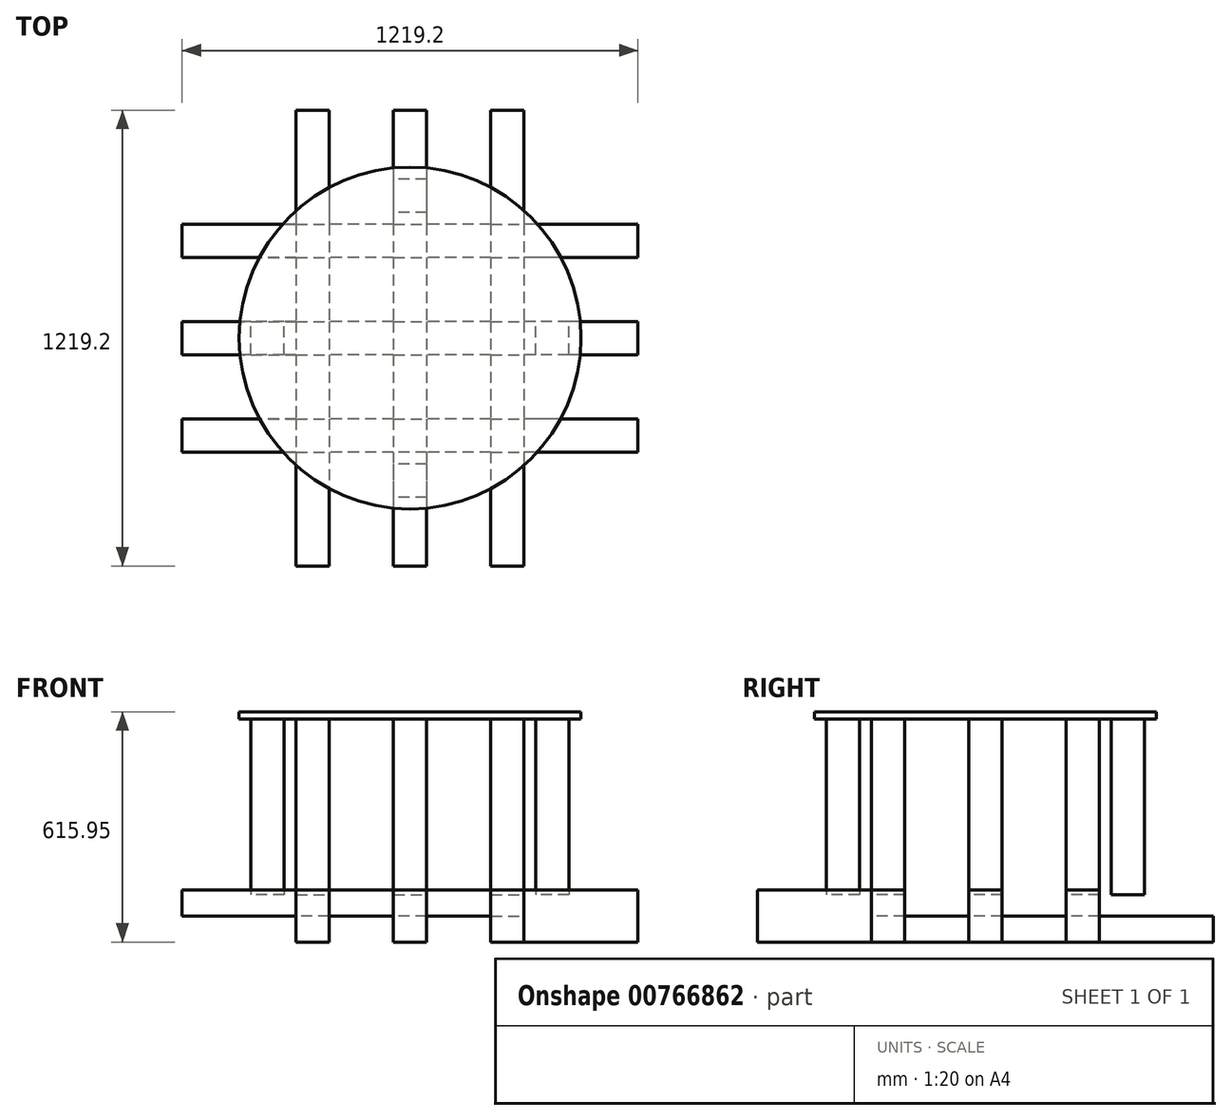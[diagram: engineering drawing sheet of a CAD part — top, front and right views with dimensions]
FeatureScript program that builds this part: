
annotation { "Feature Type Name" : "Feature", "Feature Type Description" : "" }
export const myFeature = defineFeature(function(context is Context, id is Id, definition is map)
    precondition{}
    {
        {
            var Q0;
            Q0=qCreatedBy(makeId("Top.planeOp"),FACE);
            var sketch = newSketch(context, id + "F0", { "sketchPlane" : qUnion([Q0])});
            skCircle(sketch, "E0", {"center": v(0, 0) * mm, "radius": 381 * mm, "construction": true});
            skLineSegment(sketch, "E1.bottom", {"start": v(-44.45, 609.6) * mm, "end": v(44.45, 609.6) * mm});
            skLineSegment(sketch, "E1.top", {"start": v(-44.45, -609.6) * mm, "end": v(44.45, -609.6) * mm});
            skLineSegment(sketch, "E1.left", {"start": v(-44.45, 609.6) * mm, "end": v(-44.45, -609.6) * mm});
            skLineSegment(sketch, "E1.right", {"start": v(44.45, 609.6) * mm, "end": v(44.45, -609.6) * mm});
            skLineSegment(sketch, "E2", {"start": v(0, 0) * mm, "end": v(260.35, 0) * mm, "construction": true});
            skLineSegment(sketch, "E3", {"start": v(0, 0) * mm, "end": v(-260.35, 0) * mm, "construction": true});
            skPoint(sketch, "E3.endSnap0", {"position": v(-44.45, 0) * mm});
            skLineSegment(sketch, "E4.bottom", {"start": v(-304.8, 609.6) * mm, "end": v(-215.9, 609.6) * mm});
            skLineSegment(sketch, "E4.top", {"start": v(-304.8, -609.6) * mm, "end": v(-215.9, -609.6) * mm});
            skLineSegment(sketch, "E4.left", {"start": v(-304.8, 609.6) * mm, "end": v(-304.8, -609.6) * mm});
            skLineSegment(sketch, "E4.right", {"start": v(-215.9, 609.6) * mm, "end": v(-215.9, -609.6) * mm});
            skPoint(sketch, "E4.middle", {"position": v(-260.35, 0) * mm});
            skLineSegment(sketch, "E5.bottom", {"start": v(215.9, 609.6) * mm, "end": v(304.8, 609.6) * mm});
            skLineSegment(sketch, "E5.top", {"start": v(215.9, -609.6) * mm, "end": v(304.8, -609.6) * mm});
            skLineSegment(sketch, "E5.left", {"start": v(215.9, 609.6) * mm, "end": v(215.9, -609.6) * mm});
            skLineSegment(sketch, "E5.right", {"start": v(304.8, 609.6) * mm, "end": v(304.8, -304.8) * mm});
            skPoint(sketch, "E5.middle", {"position": v(260.35, 0) * mm});
            skPoint(sketch, "E5.cornerSnap0", {"position": v(-260.35, 609.6) * mm});
            skLineSegment(sketch, "E6", {"start": v(0, 0) * mm, "end": v(0, 260.35) * mm, "construction": true});
            skLineSegment(sketch, "E7", {"start": v(0, 0) * mm, "end": v(0, -260.35) * mm, "construction": true});
            skLineSegment(sketch, "E8.bottom", {"start": v(609.6, 304.8) * mm, "end": v(-304.8, 304.8) * mm});
            skLineSegment(sketch, "E8.top", {"start": v(609.6, 215.9) * mm, "end": v(-609.6, 215.9) * mm});
            skLineSegment(sketch, "E8.left", {"start": v(609.6, 304.8) * mm, "end": v(609.6, 215.9) * mm});
            skLineSegment(sketch, "E8.right", {"start": v(-609.6, 304.8) * mm, "end": v(-609.6, 215.9) * mm});
            skPoint(sketch, "E8.middle", {"position": v(0, 260.35) * mm});
            skLineSegment(sketch, "E9.bottom", {"start": v(609.6, -215.9) * mm, "end": v(-609.6, -215.9) * mm});
            skLineSegment(sketch, "E9.top", {"start": v(609.6, -304.8) * mm, "end": v(-609.6, -304.8) * mm});
            skLineSegment(sketch, "E9.left", {"start": v(609.6, -215.9) * mm, "end": v(609.6, -304.8) * mm});
            skLineSegment(sketch, "E9.right", {"start": v(-609.6, -215.9) * mm, "end": v(-609.6, -304.8) * mm});
            skPoint(sketch, "E9.middle", {"position": v(0, -260.35) * mm});
            skLineSegment(sketch, "E10.bottom", {"start": v(609.6, 44.45) * mm, "end": v(-609.6, 44.45) * mm});
            skLineSegment(sketch, "E10.top", {"start": v(609.6, -44.45) * mm, "end": v(-609.6, -44.45) * mm});
            skLineSegment(sketch, "E10.left", {"start": v(609.6, 44.45) * mm, "end": v(609.6, -44.45) * mm});
            skLineSegment(sketch, "E10.right", {"start": v(-609.6, 44.45) * mm, "end": v(-609.6, -44.45) * mm});
            skLineSegment(sketch, "E11", {"start": v(-304.8, 304.8) * mm, "end": v(-609.6, 304.8) * mm});
            skLineSegment(sketch, "E12", {"start": v(304.8, -304.8) * mm, "end": v(304.8, -609.6) * mm});
            skSolve(sketch);
        }
        {
            var Q0;
            {var subQ0=sQuery(id+"F0.wireOp",EDGE,"E4.bottom");Q0=makeQuery(id+"F0.imprint","IMPRINT",FACE,{"disambiguationData":[TD([[makeQuery(id+"F0.imprint","IMPRINT",EDGE,{"derivedFrom":subQ0}),-1.0]])]});}
            var Q1;
            {var subQ0=sQuery(id+"F0.wireOp",EDGE,"E8.bottom");var subQ5=sQuery(id+"F0.wireOp",EDGE,"E4.right");var subQ6=makeQuery(id+"F0.imprint","INTERSECT",VERTEX,{"derivedFrom":[subQ5,subQ0]});Q1=makeQuery(id+"F0.imprint","IMPRINT",FACE,{"disambiguationData":[TD([[makeQuery(id+"F0.imprint","IMPRINT",EDGE,{"disambiguationData":[TD([[subQ6,-1.0]])],"derivedFrom":subQ5}),-1.0]])]});}
            var Q2;
            {var subQ0=sQuery(id+"F0.wireOp",EDGE,"E8.top");var subQ1=sQuery(id+"F0.wireOp",EDGE,"E4.left");var subQ2=makeQuery(id+"F0.imprint","INTERSECT",VERTEX,{"derivedFrom":[subQ1,subQ0]});Q2=makeQuery(id+"F0.imprint","IMPRINT",FACE,{"disambiguationData":[TD([[makeQuery(id+"F0.imprint","IMPRINT",EDGE,{"disambiguationData":[TD([[subQ2,-1.0]])],"derivedFrom":subQ1}),1.0]])]});}
            var Q3;
            {var subQ0=sQuery(id+"F0.wireOp",EDGE,"E10.bottom");var subQ1=sQuery(id+"F0.wireOp",EDGE,"E4.left");var subQ2=makeQuery(id+"F0.imprint","INTERSECT",VERTEX,{"derivedFrom":[subQ1,subQ0]});Q3=makeQuery(id+"F0.imprint","IMPRINT",FACE,{"disambiguationData":[TD([[makeQuery(id+"F0.imprint","IMPRINT",EDGE,{"disambiguationData":[TD([[subQ2,-1.0]])],"derivedFrom":subQ1}),1.0]])]});}
            var Q4;
            {var subQ0=sQuery(id+"F0.wireOp",EDGE,"E10.top");var subQ1=sQuery(id+"F0.wireOp",EDGE,"E4.left");var subQ2=makeQuery(id+"F0.imprint","INTERSECT",VERTEX,{"derivedFrom":[subQ1,subQ0]});Q4=makeQuery(id+"F0.imprint","IMPRINT",FACE,{"disambiguationData":[TD([[makeQuery(id+"F0.imprint","IMPRINT",EDGE,{"disambiguationData":[TD([[subQ2,-1.0]])],"derivedFrom":subQ1}),1.0]])]});}
            var Q5;
            {var subQ0=sQuery(id+"F0.wireOp",EDGE,"E9.bottom");var subQ1=sQuery(id+"F0.wireOp",EDGE,"E4.left");var subQ2=makeQuery(id+"F0.imprint","INTERSECT",VERTEX,{"derivedFrom":[subQ1,subQ0]});Q5=makeQuery(id+"F0.imprint","IMPRINT",FACE,{"disambiguationData":[TD([[makeQuery(id+"F0.imprint","IMPRINT",EDGE,{"disambiguationData":[TD([[subQ2,-1.0]])],"derivedFrom":subQ1}),1.0]])]});}
            var Q6;
            {var subQ0=sQuery(id+"F0.wireOp",EDGE,"E4.top");Q6=makeQuery(id+"F0.imprint","IMPRINT",FACE,{"disambiguationData":[TD([[makeQuery(id+"F0.imprint","IMPRINT",EDGE,{"derivedFrom":subQ0}),1.0]])]});}
            var Q7;
            {var subQ0=sQuery(id+"F0.wireOp",EDGE,"E1.top");Q7=makeQuery(id+"F0.imprint","IMPRINT",FACE,{"disambiguationData":[TD([[makeQuery(id+"F0.imprint","IMPRINT",EDGE,{"derivedFrom":subQ0}),1.0]])]});}
            var Q8;
            {var subQ0=sQuery(id+"F0.wireOp",EDGE,"E9.top");var subQ1=sQuery(id+"F0.wireOp",EDGE,"E1.left");var subQ2=makeQuery(id+"F0.imprint","INTERSECT",VERTEX,{"derivedFrom":[subQ1,subQ0]});Q8=makeQuery(id+"F0.imprint","IMPRINT",FACE,{"disambiguationData":[TD([[makeQuery(id+"F0.imprint","IMPRINT",EDGE,{"disambiguationData":[TD([[subQ2,1.0]])],"derivedFrom":subQ1}),1.0]])]});}
            var Q9;
            {var subQ0=sQuery(id+"F0.wireOp",EDGE,"E10.top");var subQ1=sQuery(id+"F0.wireOp",EDGE,"E1.left");var subQ2=makeQuery(id+"F0.imprint","INTERSECT",VERTEX,{"derivedFrom":[subQ1,subQ0]});Q9=makeQuery(id+"F0.imprint","IMPRINT",FACE,{"disambiguationData":[TD([[makeQuery(id+"F0.imprint","IMPRINT",EDGE,{"disambiguationData":[TD([[subQ2,-1.0]])],"derivedFrom":subQ1}),1.0]])]});}
            var Q10;
            {var subQ0=sQuery(id+"F0.wireOp",EDGE,"E10.bottom");var subQ1=sQuery(id+"F0.wireOp",EDGE,"E1.left");var subQ2=makeQuery(id+"F0.imprint","INTERSECT",VERTEX,{"derivedFrom":[subQ1,subQ0]});Q10=makeQuery(id+"F0.imprint","IMPRINT",FACE,{"disambiguationData":[TD([[makeQuery(id+"F0.imprint","IMPRINT",EDGE,{"disambiguationData":[TD([[subQ2,-1.0]])],"derivedFrom":subQ1}),1.0]])]});}
            var Q11;
            {var subQ0=sQuery(id+"F0.wireOp",EDGE,"E8.top");var subQ1=sQuery(id+"F0.wireOp",EDGE,"E1.left");var subQ2=makeQuery(id+"F0.imprint","INTERSECT",VERTEX,{"derivedFrom":[subQ1,subQ0]});Q11=makeQuery(id+"F0.imprint","IMPRINT",FACE,{"disambiguationData":[TD([[makeQuery(id+"F0.imprint","IMPRINT",EDGE,{"disambiguationData":[TD([[subQ2,-1.0]])],"derivedFrom":subQ1}),1.0]])]});}
            var Q12;
            {var subQ0=sQuery(id+"F0.wireOp",EDGE,"E8.bottom");var subQ1=sQuery(id+"F0.wireOp",EDGE,"E1.left");var subQ2=makeQuery(id+"F0.imprint","INTERSECT",VERTEX,{"derivedFrom":[subQ1,subQ0]});Q12=makeQuery(id+"F0.imprint","IMPRINT",FACE,{"disambiguationData":[TD([[makeQuery(id+"F0.imprint","IMPRINT",EDGE,{"disambiguationData":[TD([[subQ2,-1.0]])],"derivedFrom":subQ1}),1.0]])]});}
            var Q13;
            {var subQ0=sQuery(id+"F0.wireOp",EDGE,"E1.bottom");Q13=makeQuery(id+"F0.imprint","IMPRINT",FACE,{"disambiguationData":[TD([[makeQuery(id+"F0.imprint","IMPRINT",EDGE,{"derivedFrom":subQ0}),-1.0]])]});}
            var Q14;
            {var subQ0=sQuery(id+"F0.wireOp",EDGE,"E5.bottom");Q14=makeQuery(id+"F0.imprint","IMPRINT",FACE,{"disambiguationData":[TD([[makeQuery(id+"F0.imprint","IMPRINT",EDGE,{"derivedFrom":subQ0}),-1.0]])]});}
            var Q15;
            {var subQ0=sQuery(id+"F0.wireOp",EDGE,"E8.bottom");var subQ1=sQuery(id+"F0.wireOp",EDGE,"E5.left");var subQ2=makeQuery(id+"F0.imprint","INTERSECT",VERTEX,{"derivedFrom":[subQ1,subQ0]});Q15=makeQuery(id+"F0.imprint","IMPRINT",FACE,{"disambiguationData":[TD([[makeQuery(id+"F0.imprint","IMPRINT",EDGE,{"disambiguationData":[TD([[subQ2,-1.0]])],"derivedFrom":subQ1}),1.0]])]});}
            var Q16;
            {var subQ0=sQuery(id+"F0.wireOp",EDGE,"E8.top");var subQ1=sQuery(id+"F0.wireOp",EDGE,"E5.left");var subQ2=makeQuery(id+"F0.imprint","INTERSECT",VERTEX,{"derivedFrom":[subQ1,subQ0]});Q16=makeQuery(id+"F0.imprint","IMPRINT",FACE,{"disambiguationData":[TD([[makeQuery(id+"F0.imprint","IMPRINT",EDGE,{"disambiguationData":[TD([[subQ2,-1.0]])],"derivedFrom":subQ1}),1.0]])]});}
            var Q17;
            {var subQ0=sQuery(id+"F0.wireOp",EDGE,"E10.bottom");var subQ1=sQuery(id+"F0.wireOp",EDGE,"E5.left");var subQ2=makeQuery(id+"F0.imprint","INTERSECT",VERTEX,{"derivedFrom":[subQ1,subQ0]});Q17=makeQuery(id+"F0.imprint","IMPRINT",FACE,{"disambiguationData":[TD([[makeQuery(id+"F0.imprint","IMPRINT",EDGE,{"disambiguationData":[TD([[subQ2,-1.0]])],"derivedFrom":subQ1}),1.0]])]});}
            var Q18;
            {var subQ0=sQuery(id+"F0.wireOp",EDGE,"E10.top");var subQ1=sQuery(id+"F0.wireOp",EDGE,"E5.left");var subQ2=makeQuery(id+"F0.imprint","INTERSECT",VERTEX,{"derivedFrom":[subQ1,subQ0]});Q18=makeQuery(id+"F0.imprint","IMPRINT",FACE,{"disambiguationData":[TD([[makeQuery(id+"F0.imprint","IMPRINT",EDGE,{"disambiguationData":[TD([[subQ2,-1.0]])],"derivedFrom":subQ1}),1.0]])]});}
            var Q19;
            {var subQ0=sQuery(id+"F0.wireOp",EDGE,"E9.top");var subQ1=sQuery(id+"F0.wireOp",EDGE,"E5.left");var subQ2=makeQuery(id+"F0.imprint","INTERSECT",VERTEX,{"derivedFrom":[subQ1,subQ0]});Q19=makeQuery(id+"F0.imprint","IMPRINT",FACE,{"disambiguationData":[TD([[makeQuery(id+"F0.imprint","IMPRINT",EDGE,{"disambiguationData":[TD([[subQ2,1.0]])],"derivedFrom":subQ1}),1.0]])]});}
            var Q20;
            {var subQ0=sQuery(id+"F0.wireOp",EDGE,"E5.top");Q20=makeQuery(id+"F0.imprint","IMPRINT",FACE,{"disambiguationData":[TD([[makeQuery(id+"F0.imprint","IMPRINT",EDGE,{"derivedFrom":subQ0}),1.0]])]});}
            extrude(context, id + "F1", {"entities" : qUnion([Q0, Q1, Q2, Q3, Q4, Q5, Q6, Q7, Q8, Q9, Q10, Q11, Q12, Q13, Q14, Q15, Q16, Q17, Q18, Q19, Q20]), "depth" : 139.7 * mm, "offsetDistance" : 25.4 * mm});
        }
        {
            var Q0;
            {var subQ4=sQuery(id+"F0.wireOp",EDGE,"E8.right");Q0=makeQuery(id+"F0.imprint","IMPRINT",FACE,{"disambiguationData":[TD([[makeQuery(id+"F0.imprint","IMPRINT",EDGE,{"derivedFrom":subQ4}),1.0]])]});}
            var Q1;
            {var subQ0=sQuery(id+"F0.wireOp",EDGE,"E8.bottom");var subQ5=sQuery(id+"F0.wireOp",EDGE,"E4.right");var subQ6=makeQuery(id+"F0.imprint","INTERSECT",VERTEX,{"derivedFrom":[subQ5,subQ0]});Q1=makeQuery(id+"F0.imprint","IMPRINT",FACE,{"disambiguationData":[TD([[makeQuery(id+"F0.imprint","IMPRINT",EDGE,{"disambiguationData":[TD([[subQ6,-1.0]])],"derivedFrom":subQ5}),-1.0]])]});}
            var Q2;
            {var subQ0=sQuery(id+"F0.wireOp",EDGE,"E8.bottom");var subQ1=sQuery(id+"F0.wireOp",EDGE,"E1.left");var subQ2=makeQuery(id+"F0.imprint","INTERSECT",VERTEX,{"derivedFrom":[subQ1,subQ0]});Q2=makeQuery(id+"F0.imprint","IMPRINT",FACE,{"disambiguationData":[TD([[makeQuery(id+"F0.imprint","IMPRINT",EDGE,{"disambiguationData":[TD([[subQ2,-1.0]])],"derivedFrom":subQ1}),-1.0]])]});}
            var Q3;
            {var subQ0=sQuery(id+"F0.wireOp",EDGE,"E8.bottom");var subQ1=sQuery(id+"F0.wireOp",EDGE,"E1.left");var subQ2=makeQuery(id+"F0.imprint","INTERSECT",VERTEX,{"derivedFrom":[subQ1,subQ0]});Q3=makeQuery(id+"F0.imprint","IMPRINT",FACE,{"disambiguationData":[TD([[makeQuery(id+"F0.imprint","IMPRINT",EDGE,{"disambiguationData":[TD([[subQ2,-1.0]])],"derivedFrom":subQ1}),1.0]])]});}
            var Q4;
            {var subQ0=sQuery(id+"F0.wireOp",EDGE,"E8.bottom");var subQ1=sQuery(id+"F0.wireOp",EDGE,"E1.right");var subQ2=makeQuery(id+"F0.imprint","INTERSECT",VERTEX,{"derivedFrom":[subQ1,subQ0]});Q4=makeQuery(id+"F0.imprint","IMPRINT",FACE,{"disambiguationData":[TD([[makeQuery(id+"F0.imprint","IMPRINT",EDGE,{"disambiguationData":[TD([[subQ2,-1.0]])],"derivedFrom":subQ1}),1.0]])]});}
            var Q5;
            {var subQ0=sQuery(id+"F0.wireOp",EDGE,"E8.bottom");var subQ1=sQuery(id+"F0.wireOp",EDGE,"E5.left");var subQ2=makeQuery(id+"F0.imprint","INTERSECT",VERTEX,{"derivedFrom":[subQ1,subQ0]});Q5=makeQuery(id+"F0.imprint","IMPRINT",FACE,{"disambiguationData":[TD([[makeQuery(id+"F0.imprint","IMPRINT",EDGE,{"disambiguationData":[TD([[subQ2,-1.0]])],"derivedFrom":subQ1}),1.0]])]});}
            var Q6;
            {var subQ5=sQuery(id+"F0.wireOp",EDGE,"E8.left");Q6=makeQuery(id+"F0.imprint","IMPRINT",FACE,{"disambiguationData":[TD([[makeQuery(id+"F0.imprint","IMPRINT",EDGE,{"derivedFrom":subQ5}),-1.0]])]});}
            var Q7;
            {var subQ5=sQuery(id+"F0.wireOp",EDGE,"E10.left");Q7=makeQuery(id+"F0.imprint","IMPRINT",FACE,{"disambiguationData":[TD([[makeQuery(id+"F0.imprint","IMPRINT",EDGE,{"derivedFrom":subQ5}),-1.0]])]});}
            var Q8;
            {var subQ0=sQuery(id+"F0.wireOp",EDGE,"E10.bottom");var subQ1=sQuery(id+"F0.wireOp",EDGE,"E5.left");var subQ2=makeQuery(id+"F0.imprint","INTERSECT",VERTEX,{"derivedFrom":[subQ1,subQ0]});Q8=makeQuery(id+"F0.imprint","IMPRINT",FACE,{"disambiguationData":[TD([[makeQuery(id+"F0.imprint","IMPRINT",EDGE,{"disambiguationData":[TD([[subQ2,-1.0]])],"derivedFrom":subQ1}),1.0]])]});}
            var Q9;
            {var subQ0=sQuery(id+"F0.wireOp",EDGE,"E10.bottom");var subQ1=sQuery(id+"F0.wireOp",EDGE,"E1.right");var subQ2=makeQuery(id+"F0.imprint","INTERSECT",VERTEX,{"derivedFrom":[subQ1,subQ0]});Q9=makeQuery(id+"F0.imprint","IMPRINT",FACE,{"disambiguationData":[TD([[makeQuery(id+"F0.imprint","IMPRINT",EDGE,{"disambiguationData":[TD([[subQ2,-1.0]])],"derivedFrom":subQ1}),1.0]])]});}
            var Q10;
            {var subQ0=sQuery(id+"F0.wireOp",EDGE,"E10.bottom");var subQ1=sQuery(id+"F0.wireOp",EDGE,"E1.left");var subQ2=makeQuery(id+"F0.imprint","INTERSECT",VERTEX,{"derivedFrom":[subQ1,subQ0]});Q10=makeQuery(id+"F0.imprint","IMPRINT",FACE,{"disambiguationData":[TD([[makeQuery(id+"F0.imprint","IMPRINT",EDGE,{"disambiguationData":[TD([[subQ2,-1.0]])],"derivedFrom":subQ1}),1.0]])]});}
            var Q11;
            {var subQ0=sQuery(id+"F0.wireOp",EDGE,"E10.bottom");var subQ1=sQuery(id+"F0.wireOp",EDGE,"E1.left");var subQ2=makeQuery(id+"F0.imprint","INTERSECT",VERTEX,{"derivedFrom":[subQ1,subQ0]});Q11=makeQuery(id+"F0.imprint","IMPRINT",FACE,{"disambiguationData":[TD([[makeQuery(id+"F0.imprint","IMPRINT",EDGE,{"disambiguationData":[TD([[subQ2,-1.0]])],"derivedFrom":subQ1}),-1.0]])]});}
            var Q12;
            {var subQ0=sQuery(id+"F0.wireOp",EDGE,"E10.bottom");var subQ1=sQuery(id+"F0.wireOp",EDGE,"E4.left");var subQ2=makeQuery(id+"F0.imprint","INTERSECT",VERTEX,{"derivedFrom":[subQ1,subQ0]});Q12=makeQuery(id+"F0.imprint","IMPRINT",FACE,{"disambiguationData":[TD([[makeQuery(id+"F0.imprint","IMPRINT",EDGE,{"disambiguationData":[TD([[subQ2,-1.0]])],"derivedFrom":subQ1}),1.0]])]});}
            var Q13;
            {var subQ5=sQuery(id+"F0.wireOp",EDGE,"E10.right");Q13=makeQuery(id+"F0.imprint","IMPRINT",FACE,{"disambiguationData":[TD([[makeQuery(id+"F0.imprint","IMPRINT",EDGE,{"derivedFrom":subQ5}),1.0]])]});}
            var Q14;
            {var subQ5=sQuery(id+"F0.wireOp",EDGE,"E9.right");Q14=makeQuery(id+"F0.imprint","IMPRINT",FACE,{"disambiguationData":[TD([[makeQuery(id+"F0.imprint","IMPRINT",EDGE,{"derivedFrom":subQ5}),1.0]])]});}
            var Q15;
            {var subQ0=sQuery(id+"F0.wireOp",EDGE,"E9.bottom");var subQ1=sQuery(id+"F0.wireOp",EDGE,"E4.left");var subQ2=makeQuery(id+"F0.imprint","INTERSECT",VERTEX,{"derivedFrom":[subQ1,subQ0]});Q15=makeQuery(id+"F0.imprint","IMPRINT",FACE,{"disambiguationData":[TD([[makeQuery(id+"F0.imprint","IMPRINT",EDGE,{"disambiguationData":[TD([[subQ2,-1.0]])],"derivedFrom":subQ1}),1.0]])]});}
            var Q16;
            {var subQ0=sQuery(id+"F0.wireOp",EDGE,"E9.top");var subQ1=sQuery(id+"F0.wireOp",EDGE,"E1.left");var subQ2=makeQuery(id+"F0.imprint","INTERSECT",VERTEX,{"derivedFrom":[subQ1,subQ0]});Q16=makeQuery(id+"F0.imprint","IMPRINT",FACE,{"disambiguationData":[TD([[makeQuery(id+"F0.imprint","IMPRINT",EDGE,{"disambiguationData":[TD([[subQ2,1.0]])],"derivedFrom":subQ1}),-1.0]])]});}
            var Q17;
            {var subQ0=sQuery(id+"F0.wireOp",EDGE,"E9.top");var subQ1=sQuery(id+"F0.wireOp",EDGE,"E1.left");var subQ2=makeQuery(id+"F0.imprint","INTERSECT",VERTEX,{"derivedFrom":[subQ1,subQ0]});Q17=makeQuery(id+"F0.imprint","IMPRINT",FACE,{"disambiguationData":[TD([[makeQuery(id+"F0.imprint","IMPRINT",EDGE,{"disambiguationData":[TD([[subQ2,1.0]])],"derivedFrom":subQ1}),1.0]])]});}
            var Q18;
            {var subQ0=sQuery(id+"F0.wireOp",EDGE,"E9.top");var subQ1=sQuery(id+"F0.wireOp",EDGE,"E1.right");var subQ2=makeQuery(id+"F0.imprint","INTERSECT",VERTEX,{"derivedFrom":[subQ1,subQ0]});Q18=makeQuery(id+"F0.imprint","IMPRINT",FACE,{"disambiguationData":[TD([[makeQuery(id+"F0.imprint","IMPRINT",EDGE,{"disambiguationData":[TD([[subQ2,1.0]])],"derivedFrom":subQ1}),1.0]])]});}
            var Q19;
            {var subQ0=sQuery(id+"F0.wireOp",EDGE,"E9.top");var subQ1=sQuery(id+"F0.wireOp",EDGE,"E5.left");var subQ2=makeQuery(id+"F0.imprint","INTERSECT",VERTEX,{"derivedFrom":[subQ1,subQ0]});Q19=makeQuery(id+"F0.imprint","IMPRINT",FACE,{"disambiguationData":[TD([[makeQuery(id+"F0.imprint","IMPRINT",EDGE,{"disambiguationData":[TD([[subQ2,1.0]])],"derivedFrom":subQ1}),1.0]])]});}
            var Q20;
            {var subQ5=sQuery(id+"F0.wireOp",EDGE,"E9.left");Q20=makeQuery(id+"F0.imprint","IMPRINT",FACE,{"disambiguationData":[TD([[makeQuery(id+"F0.imprint","IMPRINT",EDGE,{"derivedFrom":subQ5}),-1.0]])]});}
            extrude(context, id + "F2", {"entities" : qUnion([Q0, Q1, Q2, Q3, Q4, Q5, Q6, Q7, Q8, Q9, Q10, Q11, Q12, Q13, Q14, Q15, Q16, Q17, Q18, Q19, Q20]), "depth" : 139.7 * mm, "offsetDistance" : 25.4 * mm});
        }
        {
            var Q0;
            Q0=makeQuery(id+"F2.opExtrude","SWEPT_FACE",FACE,{"disambiguationData":[OSD([sQuery(id+"F0.wireOp",EDGE,"E9.top")])]});
            var sketch = newSketch(context, id + "F3", { "sketchPlane" : qUnion([Q0])});
            skLineSegment(sketch, "E13.0", {"start": v(-304.8, 139.7) * mm, "end": v(-304.8, 69.85) * mm});
            skLineSegment(sketch, "E14.0", {"start": v(-215.9, 139.7) * mm, "end": v(-215.9, 69.85) * mm});
            skLineSegment(sketch, "E15.0", {"start": v(-44.45, 139.7) * mm, "end": v(-44.45, 69.85) * mm});
            skLineSegment(sketch, "E16.0", {"start": v(44.45, 139.7) * mm, "end": v(44.45, 69.85) * mm});
            skLineSegment(sketch, "E17.0", {"start": v(215.9, 139.7) * mm, "end": v(215.9, 69.85) * mm});
            skLineSegment(sketch, "E18.0", {"start": v(304.8, 139.7) * mm, "end": v(304.8, 69.85) * mm});
            skLineSegment(sketch, "E19", {"start": v(-304.8, 69.85) * mm, "end": v(-215.9, 69.85) * mm});
            skLineSegment(sketch, "E20", {"start": v(-44.45, 69.85) * mm, "end": v(44.45, 69.85) * mm});
            skLineSegment(sketch, "E21", {"start": v(215.9, 69.85) * mm, "end": v(304.8, 69.85) * mm});
            skPoint(sketch, "E22.orphan", {"position": v(-304.8, 0) * mm});
            skPoint(sketch, "E23.orphan", {"position": v(-215.9, 0) * mm});
            skPoint(sketch, "E24.orphan", {"position": v(-44.45, 0) * mm});
            skPoint(sketch, "E25.orphan", {"position": v(44.45, 0) * mm});
            skPoint(sketch, "E26.orphan", {"position": v(215.9, 0) * mm});
            skPoint(sketch, "E27.orphan", {"position": v(304.8, 0) * mm});
            skSolve(sketch);
        }
        {
            var Q0;
            {var subQ0=sQuery(id+"F3.wireOp",EDGE,"E13.0");Q0=makeQuery(id+"F3.imprint","IMPRINT",FACE,{"disambiguationData":[TD([[makeQuery(id+"F3.imprint","IMPRINT",EDGE,{"derivedFrom":subQ0}),1.0]])]});}
            var Q1;
            {var subQ0=sQuery(id+"F3.wireOp",EDGE,"E15.0");Q1=makeQuery(id+"F3.imprint","IMPRINT",FACE,{"disambiguationData":[TD([[makeQuery(id+"F3.imprint","IMPRINT",EDGE,{"derivedFrom":subQ0}),1.0]])]});}
            var Q2;
            {var subQ0=sQuery(id+"F3.wireOp",EDGE,"E17.0");Q2=makeQuery(id+"F3.imprint","IMPRINT",FACE,{"disambiguationData":[TD([[makeQuery(id+"F3.imprint","IMPRINT",EDGE,{"derivedFrom":subQ0}),1.0]])]});}
            extrude(context, id + "F4", {"entities" : qUnion([Q0, Q1, Q2]), "operationType" : NewBodyOperationType.REMOVE, "endBound" : BoundingType.THROUGH_ALL, "oppositeDirection" : true, "depth" : 25.4 * mm, "offsetDistance" : 25.4 * mm});
        }
        {
            var Q0;
            Q0=makeQuery(id+"F1.opExtrude","SWEPT_FACE",FACE,{"disambiguationData":[OSD([sQuery(id+"F0.wireOp",EDGE,"E5.right"),sQuery(id+"F0.wireOp",EDGE,"E12")])]});
            var sketch = newSketch(context, id + "F5", { "sketchPlane" : qUnion([Q0])});
            skLineSegment(sketch, "E28.0", {"start": v(-304.8, 69.85) * mm, "end": v(-304.8, 0) * mm});
            skLineSegment(sketch, "E29.0", {"start": v(-215.9, 69.85) * mm, "end": v(-215.9, 0) * mm});
            skLineSegment(sketch, "E30.0", {"start": v(-44.45, 69.85) * mm, "end": v(-44.45, 0) * mm});
            skLineSegment(sketch, "E31.0", {"start": v(44.45, 69.85) * mm, "end": v(44.45, 0) * mm});
            skLineSegment(sketch, "E32.0", {"start": v(215.9, 69.85) * mm, "end": v(215.9, 0) * mm});
            skLineSegment(sketch, "E33.0", {"start": v(304.8, 69.85) * mm, "end": v(304.8, 0) * mm});
            skLineSegment(sketch, "E34", {"start": v(-304.8, 69.85) * mm, "end": v(-215.9, 69.85) * mm});
            skLineSegment(sketch, "E35", {"start": v(-44.45, 69.85) * mm, "end": v(44.45, 69.85) * mm});
            skLineSegment(sketch, "E36", {"start": v(215.9, 69.85) * mm, "end": v(304.8, 69.85) * mm});
            skPoint(sketch, "E37.orphan", {"position": v(-304.8, 139.7) * mm});
            skPoint(sketch, "E38.orphan", {"position": v(-215.9, 139.7) * mm});
            skPoint(sketch, "E39.orphan", {"position": v(-44.45, 139.7) * mm});
            skPoint(sketch, "E40.orphan", {"position": v(44.45, 139.7) * mm});
            skPoint(sketch, "E41.orphan", {"position": v(215.9, 139.7) * mm});
            skPoint(sketch, "E42.orphan", {"position": v(304.8, 139.7) * mm});
            skSolve(sketch);
        }
        {
            var Q0;
            {var subQ0=sQuery(id+"F5.wireOp",EDGE,"E28.0");Q0=makeQuery(id+"F5.imprint","IMPRINT",FACE,{"disambiguationData":[TD([[makeQuery(id+"F5.imprint","IMPRINT",EDGE,{"derivedFrom":subQ0}),1.0]])]});}
            var Q1;
            {var subQ0=sQuery(id+"F5.wireOp",EDGE,"E30.0");Q1=makeQuery(id+"F5.imprint","IMPRINT",FACE,{"disambiguationData":[TD([[makeQuery(id+"F5.imprint","IMPRINT",EDGE,{"derivedFrom":subQ0}),1.0]])]});}
            var Q2;
            {var subQ0=sQuery(id+"F5.wireOp",EDGE,"E32.0");Q2=makeQuery(id+"F5.imprint","IMPRINT",FACE,{"disambiguationData":[TD([[makeQuery(id+"F5.imprint","IMPRINT",EDGE,{"derivedFrom":subQ0}),1.0]])]});}
            extrude(context, id + "F6", {"entities" : qUnion([Q0, Q1, Q2]), "operationType" : NewBodyOperationType.REMOVE, "endBound" : BoundingType.THROUGH_ALL, "oppositeDirection" : true, "depth" : 25.4 * mm, "offsetDistance" : 25.4 * mm});
        }
        {
            var Q0;
            Q0=makeQuery(id+"F1.opExtrude","CAP_FACE",FACE,{"disambiguationData":[OSD([sQuery(id+"F0.wireOp",EDGE,"E1.bottom"),sQuery(id+"F0.wireOp",EDGE,"E1.top"),sQuery(id+"F0.wireOp",EDGE,"E1.left"),sQuery(id+"F0.wireOp",EDGE,"E1.right")])],"isStart":false});
            var sketch = newSketch(context, id + "F7", { "sketchPlane" : qUnion([Q0])});
            skLineSegment(sketch, "E43.0", {"start": v(609.6, 304.8) * mm, "end": v(-304.8, 304.8) * mm, "construction": true});
            skLineSegment(sketch, "E43.1", {"start": v(-304.8, 304.8) * mm, "end": v(-609.6, 304.8) * mm, "construction": true});
            skLineSegment(sketch, "E43.2", {"start": v(609.6, 215.9) * mm, "end": v(-609.6, 215.9) * mm, "construction": true});
            skLineSegment(sketch, "E43.5", {"start": v(609.6, -215.9) * mm, "end": v(-609.6, -215.9) * mm, "construction": true});
            skLineSegment(sketch, "E43.6", {"start": v(609.6, -304.8) * mm, "end": v(-609.6, -304.8) * mm, "construction": true});
            skLineSegment(sketch, "E43.9", {"start": v(215.9, 609.6) * mm, "end": v(215.9, -609.6) * mm, "construction": true});
            skLineSegment(sketch, "E43.10", {"start": v(304.8, 609.6) * mm, "end": v(304.8, -304.8) * mm, "construction": true});
            skLineSegment(sketch, "E43.11", {"start": v(304.8, -304.8) * mm, "end": v(304.8, -609.6) * mm, "construction": true});
            skLineSegment(sketch, "E43.12", {"start": v(-215.9, 609.6) * mm, "end": v(-215.9, -609.6) * mm, "construction": true});
            skLineSegment(sketch, "E43.13", {"start": v(-304.8, 609.6) * mm, "end": v(-304.8, -609.6) * mm, "construction": true});
            skLineSegment(sketch, "E44.bottom", {"start": v(-304.8, 304.8) * mm, "end": v(-215.9, 304.8) * mm});
            skLineSegment(sketch, "E44.top", {"start": v(-304.8, 215.9) * mm, "end": v(-215.9, 215.9) * mm});
            skLineSegment(sketch, "E44.left", {"start": v(-304.8, 304.8) * mm, "end": v(-304.8, 215.9) * mm});
            skLineSegment(sketch, "E44.right", {"start": v(-215.9, 304.8) * mm, "end": v(-215.9, 215.9) * mm});
            skLineSegment(sketch, "E45.bottom", {"start": v(-44.45, 304.8) * mm, "end": v(44.45, 304.8) * mm, "construction": true});
            skLineSegment(sketch, "E45.top", {"start": v(-44.45, 215.9) * mm, "end": v(44.45, 215.9) * mm, "construction": true});
            skLineSegment(sketch, "E46.bottom", {"start": v(215.9, 304.8) * mm, "end": v(304.8, 304.8) * mm});
            skLineSegment(sketch, "E46.top", {"start": v(215.9, 215.9) * mm, "end": v(304.8, 215.9) * mm});
            skLineSegment(sketch, "E46.left", {"start": v(215.9, 304.8) * mm, "end": v(215.9, 215.9) * mm});
            skLineSegment(sketch, "E46.right", {"start": v(304.8, 304.8) * mm, "end": v(304.8, 215.9) * mm});
            skLineSegment(sketch, "E47.bottom", {"start": v(-304.8, 44.45) * mm, "end": v(-215.9, 44.45) * mm, "construction": true});
            skLineSegment(sketch, "E47.top", {"start": v(-304.8, -44.45) * mm, "end": v(-215.9, -44.45) * mm, "construction": true});
            skLineSegment(sketch, "E47.left", {"start": v(-304.8, 44.45) * mm, "end": v(-304.8, -44.45) * mm, "construction": true});
            skLineSegment(sketch, "E47.right", {"start": v(-215.9, 44.45) * mm, "end": v(-215.9, -44.45) * mm, "construction": true});
            skLineSegment(sketch, "E48.bottom", {"start": v(-44.45, 44.45) * mm, "end": v(44.45, 44.45) * mm});
            skLineSegment(sketch, "E48.top", {"start": v(-44.45, -44.45) * mm, "end": v(44.45, -44.45) * mm});
            skLineSegment(sketch, "E48.left", {"start": v(-44.45, 44.45) * mm, "end": v(-44.45, -44.45) * mm});
            skLineSegment(sketch, "E48.right", {"start": v(44.45, 44.45) * mm, "end": v(44.45, -44.45) * mm});
            skLineSegment(sketch, "E49.top", {"start": v(215.9, -44.45) * mm, "end": v(304.8, -44.45) * mm, "construction": true});
            skLineSegment(sketch, "E49.left", {"start": v(215.9, 44.45) * mm, "end": v(215.9, -44.45) * mm, "construction": true});
            skLineSegment(sketch, "E49.right", {"start": v(304.8, 44.45) * mm, "end": v(304.8, -44.45) * mm, "construction": true});
            skLineSegment(sketch, "E50.bottom", {"start": v(-304.8, -215.9) * mm, "end": v(-215.9, -215.9) * mm});
            skLineSegment(sketch, "E50.top", {"start": v(-304.8, -304.8) * mm, "end": v(-215.9, -304.8) * mm});
            skLineSegment(sketch, "E50.left", {"start": v(-304.8, -215.9) * mm, "end": v(-304.8, -304.8) * mm});
            skLineSegment(sketch, "E50.right", {"start": v(-215.9, -215.9) * mm, "end": v(-215.9, -304.8) * mm});
            skLineSegment(sketch, "E51.bottom", {"start": v(-44.45, -215.9) * mm, "end": v(44.45, -215.9) * mm, "construction": true});
            skLineSegment(sketch, "E51.top", {"start": v(-44.45, -304.8) * mm, "end": v(44.45, -304.8) * mm, "construction": true});
            skLineSegment(sketch, "E52.bottom", {"start": v(215.9, -215.9) * mm, "end": v(304.8, -215.9) * mm});
            skLineSegment(sketch, "E52.top", {"start": v(215.9, -304.8) * mm, "end": v(304.8, -304.8) * mm});
            skLineSegment(sketch, "E52.left", {"start": v(215.9, -215.9) * mm, "end": v(215.9, -304.8) * mm});
            skLineSegment(sketch, "E52.right", {"start": v(304.8, -215.9) * mm, "end": v(304.8, -304.8) * mm});
            skCircle(sketch, "E53.0", {"center": v(0, 0) * mm, "radius": 381 * mm, "construction": true});
            skLineSegment(sketch, "E54.bottom", {"start": v(44.45, -336.55) * mm, "end": v(-44.45, -336.55) * mm});
            skLineSegment(sketch, "E54.top", {"start": v(44.45, -425.45) * mm, "end": v(-44.45, -425.45) * mm});
            skLineSegment(sketch, "E54.left", {"start": v(44.45, -336.55) * mm, "end": v(44.45, -425.45) * mm});
            skLineSegment(sketch, "E54.right", {"start": v(-44.45, -336.55) * mm, "end": v(-44.45, -425.45) * mm});
            skPoint(sketch, "E54.middle", {"position": v(0, -381) * mm});
            skLineSegment(sketch, "E55.bottom", {"start": v(44.45, 425.45) * mm, "end": v(-44.45, 425.45) * mm});
            skLineSegment(sketch, "E55.top", {"start": v(44.45, 336.55) * mm, "end": v(-44.45, 336.55) * mm});
            skLineSegment(sketch, "E55.left", {"start": v(44.45, 425.45) * mm, "end": v(44.45, 336.55) * mm});
            skLineSegment(sketch, "E55.right", {"start": v(-44.45, 425.45) * mm, "end": v(-44.45, 336.55) * mm});
            skPoint(sketch, "E55.middle", {"position": v(0, 381) * mm});
            skLineSegment(sketch, "E56.bottom", {"start": v(425.45, 44.45) * mm, "end": v(336.55, 44.45) * mm});
            skLineSegment(sketch, "E56.top", {"start": v(425.45, -44.45) * mm, "end": v(336.55, -44.45) * mm});
            skLineSegment(sketch, "E56.left", {"start": v(425.45, 44.45) * mm, "end": v(425.45, -44.45) * mm});
            skLineSegment(sketch, "E56.right", {"start": v(336.55, 44.45) * mm, "end": v(336.55, -44.45) * mm});
            skPoint(sketch, "E56.middle", {"position": v(381, 0) * mm});
            skLineSegment(sketch, "E57.bottom", {"start": v(-336.55, 44.45) * mm, "end": v(-425.45, 44.45) * mm});
            skLineSegment(sketch, "E57.top", {"start": v(-336.55, -44.45) * mm, "end": v(-425.45, -44.45) * mm});
            skLineSegment(sketch, "E57.left", {"start": v(-336.55, 44.45) * mm, "end": v(-336.55, -44.45) * mm});
            skLineSegment(sketch, "E57.right", {"start": v(-425.45, 44.45) * mm, "end": v(-425.45, -44.45) * mm});
            skPoint(sketch, "E57.middle", {"position": v(-381, 0) * mm});
            skSolve(sketch);
        }
        {
            var Q0;
            Q0=makeQuery(id+"F7.imprint","IMPRINT",FACE,{"disambiguationData":[TD([[makeQuery(id+"F7.imprint","IMPRINT",EDGE,{"derivedFrom":sQuery(id+"F7.wireOp",EDGE,"E44.bottom")}),-1.0]])]});
            var Q1;
            Q1=makeQuery(id+"F7.imprint","IMPRINT",FACE,{"disambiguationData":[TD([[makeQuery(id+"F7.imprint","IMPRINT",EDGE,{"derivedFrom":sQuery(id+"F7.wireOp",EDGE,"E45.bottom")}),-1.0]])]});
            var Q2;
            Q2=makeQuery(id+"F7.imprint","IMPRINT",FACE,{"disambiguationData":[TD([[makeQuery(id+"F7.imprint","IMPRINT",EDGE,{"derivedFrom":sQuery(id+"F7.wireOp",EDGE,"E46.bottom")}),-1.0]])]});
            var Q3;
            Q3=makeQuery(id+"F7.imprint","IMPRINT",FACE,{"disambiguationData":[TD([[makeQuery(id+"F7.imprint","IMPRINT",EDGE,{"derivedFrom":sQuery(id+"F7.wireOp",EDGE,"E49.bottom")}),-1.0]])]});
            var Q4;
            Q4=makeQuery(id+"F7.imprint","IMPRINT",FACE,{"disambiguationData":[TD([[makeQuery(id+"F7.imprint","IMPRINT",EDGE,{"derivedFrom":sQuery(id+"F7.wireOp",EDGE,"E48.bottom")}),-1.0]])]});
            var Q5;
            Q5=makeQuery(id+"F7.imprint","IMPRINT",FACE,{"disambiguationData":[TD([[makeQuery(id+"F7.imprint","IMPRINT",EDGE,{"derivedFrom":sQuery(id+"F7.wireOp",EDGE,"E47.bottom")}),-1.0]])]});
            var Q6;
            Q6=makeQuery(id+"F7.imprint","IMPRINT",FACE,{"disambiguationData":[TD([[makeQuery(id+"F7.imprint","IMPRINT",EDGE,{"derivedFrom":sQuery(id+"F7.wireOp",EDGE,"E50.bottom")}),-1.0]])]});
            var Q7;
            Q7=makeQuery(id+"F7.imprint","IMPRINT",FACE,{"disambiguationData":[TD([[makeQuery(id+"F7.imprint","IMPRINT",EDGE,{"derivedFrom":sQuery(id+"F7.wireOp",EDGE,"E51.bottom")}),-1.0]])]});
            var Q8;
            Q8=makeQuery(id+"F7.imprint","IMPRINT",FACE,{"disambiguationData":[TD([[makeQuery(id+"F7.imprint","IMPRINT",EDGE,{"derivedFrom":sQuery(id+"F7.wireOp",EDGE,"E52.bottom")}),-1.0]])]});
            var Q9;
            Q9=makeQuery(id+"F7.imprint","IMPRINT",FACE,{"disambiguationData":[TD([[makeQuery(id+"F7.imprint","IMPRINT",EDGE,{"derivedFrom":sQuery(id+"F7.wireOp",EDGE,"E57.bottom")}),1.0]])]});
            var Q10;
            Q10=makeQuery(id+"F7.imprint","IMPRINT",FACE,{"disambiguationData":[TD([[makeQuery(id+"F7.imprint","IMPRINT",EDGE,{"derivedFrom":sQuery(id+"F7.wireOp",EDGE,"E56.bottom")}),1.0]])]});
            var Q11;
            Q11=makeQuery(id+"F7.imprint","IMPRINT",FACE,{"disambiguationData":[TD([[makeQuery(id+"F7.imprint","IMPRINT",EDGE,{"derivedFrom":sQuery(id+"F7.wireOp",EDGE,"E54.bottom")}),1.0]])]});
            var Q12;
            Q12=makeQuery(id+"F7.imprint","IMPRINT",FACE,{"disambiguationData":[TD([[makeQuery(id+"F7.imprint","IMPRINT",EDGE,{"derivedFrom":sQuery(id+"F7.wireOp",EDGE,"E55.bottom")}),1.0]])]});
            extrude(context, id + "F8", {"entities" : qUnion([Q0, Q1, Q2, Q3, Q4, Q5, Q6, Q7, Q8, Q9, Q10, Q11, Q12]), "depth" : 457.2 * mm, "offsetDistance" : 25.4 * mm, "hasSecondDirection" : true, "secondDirectionOppositeDirection" : true, "secondDirectionDepth" : 12.7 * mm});
        }
        {
            var Q0;
            Q0=makeQuery(id+"F8.opExtrude","SWEPT_BODY",BODY,{"disambiguationData":[OSD([sQuery(id+"F7.wireOp",EDGE,"E57.bottom"),sQuery(id+"F7.wireOp",EDGE,"E57.top"),sQuery(id+"F7.wireOp",EDGE,"E57.left"),sQuery(id+"F7.wireOp",EDGE,"E57.right")])]});
            var Q1;
            Q1=makeQuery(id+"F8.opExtrude","SWEPT_BODY",BODY,{"disambiguationData":[OSD([sQuery(id+"F7.wireOp",EDGE,"E44.bottom"),sQuery(id+"F7.wireOp",EDGE,"E44.top"),sQuery(id+"F7.wireOp",EDGE,"E44.left"),sQuery(id+"F7.wireOp",EDGE,"E44.right")])]});
            var Q2;
            Q2=makeQuery(id+"F8.opExtrude","SWEPT_BODY",BODY,{"disambiguationData":[OSD([sQuery(id+"F7.wireOp",EDGE,"E55.bottom"),sQuery(id+"F7.wireOp",EDGE,"E55.top"),sQuery(id+"F7.wireOp",EDGE,"E55.left"),sQuery(id+"F7.wireOp",EDGE,"E55.right")])]});
            var Q3;
            Q3=makeQuery(id+"F8.opExtrude","SWEPT_BODY",BODY,{"disambiguationData":[OSD([sQuery(id+"F7.wireOp",EDGE,"E46.bottom"),sQuery(id+"F7.wireOp",EDGE,"E46.top"),sQuery(id+"F7.wireOp",EDGE,"E46.left"),sQuery(id+"F7.wireOp",EDGE,"E46.right")])]});
            var Q4;
            Q4=makeQuery(id+"F8.opExtrude","SWEPT_BODY",BODY,{"disambiguationData":[OSD([sQuery(id+"F7.wireOp",EDGE,"E56.bottom"),sQuery(id+"F7.wireOp",EDGE,"E56.top"),sQuery(id+"F7.wireOp",EDGE,"E56.left"),sQuery(id+"F7.wireOp",EDGE,"E56.right")])]});
            var Q5;
            Q5=makeQuery(id+"F8.opExtrude","SWEPT_BODY",BODY,{"disambiguationData":[OSD([sQuery(id+"F7.wireOp",EDGE,"E48.bottom"),sQuery(id+"F7.wireOp",EDGE,"E48.top"),sQuery(id+"F7.wireOp",EDGE,"E48.left"),sQuery(id+"F7.wireOp",EDGE,"E48.right")])]});
            var Q6;
            Q6=makeQuery(id+"F8.opExtrude","SWEPT_BODY",BODY,{"disambiguationData":[OSD([sQuery(id+"F7.wireOp",EDGE,"E52.bottom"),sQuery(id+"F7.wireOp",EDGE,"E52.top"),sQuery(id+"F7.wireOp",EDGE,"E52.left"),sQuery(id+"F7.wireOp",EDGE,"E52.right")])]});
            var Q7;
            Q7=makeQuery(id+"F8.opExtrude","SWEPT_BODY",BODY,{"disambiguationData":[OSD([sQuery(id+"F7.wireOp",EDGE,"E54.bottom"),sQuery(id+"F7.wireOp",EDGE,"E54.top"),sQuery(id+"F7.wireOp",EDGE,"E54.left"),sQuery(id+"F7.wireOp",EDGE,"E54.right")])]});
            var Q8;
            Q8=makeQuery(id+"F8.opExtrude","SWEPT_BODY",BODY,{"disambiguationData":[OSD([sQuery(id+"F7.wireOp",EDGE,"E50.bottom"),sQuery(id+"F7.wireOp",EDGE,"E50.top"),sQuery(id+"F7.wireOp",EDGE,"E50.left"),sQuery(id+"F7.wireOp",EDGE,"E50.right")])]});
            var Q9;
            Q9=makeQuery(id+"F1.opExtrude","SWEPT_BODY",BODY,{"disambiguationData":[OSD([sQuery(id+"F0.wireOp",EDGE,"E4.bottom"),sQuery(id+"F0.wireOp",EDGE,"E4.top"),sQuery(id+"F0.wireOp",EDGE,"E4.left"),sQuery(id+"F0.wireOp",EDGE,"E4.right")])]});
            var Q10;
            Q10=makeQuery(id+"F2.opExtrude","SWEPT_BODY",BODY,{"disambiguationData":[OSD([sQuery(id+"F0.wireOp",EDGE,"E10.bottom"),sQuery(id+"F0.wireOp",EDGE,"E10.top"),sQuery(id+"F0.wireOp",EDGE,"E10.left"),sQuery(id+"F0.wireOp",EDGE,"E10.right")])]});
            var Q11;
            Q11=makeQuery(id+"F2.opExtrude","SWEPT_BODY",BODY,{"disambiguationData":[OSD([sQuery(id+"F0.wireOp",EDGE,"E8.bottom"),sQuery(id+"F0.wireOp",EDGE,"E8.top"),sQuery(id+"F0.wireOp",EDGE,"E8.left"),sQuery(id+"F0.wireOp",EDGE,"E8.right"),sQuery(id+"F0.wireOp",EDGE,"E11")])]});
            var Q12;
            Q12=makeQuery(id+"F1.opExtrude","SWEPT_BODY",BODY,{"disambiguationData":[OSD([sQuery(id+"F0.wireOp",EDGE,"E5.bottom"),sQuery(id+"F0.wireOp",EDGE,"E5.top"),sQuery(id+"F0.wireOp",EDGE,"E5.left"),sQuery(id+"F0.wireOp",EDGE,"E5.right"),sQuery(id+"F0.wireOp",EDGE,"E12")])]});
            var Q13;
            Q13=makeQuery(id+"F1.opExtrude","SWEPT_BODY",BODY,{"disambiguationData":[OSD([sQuery(id+"F0.wireOp",EDGE,"E1.bottom"),sQuery(id+"F0.wireOp",EDGE,"E1.top"),sQuery(id+"F0.wireOp",EDGE,"E1.left"),sQuery(id+"F0.wireOp",EDGE,"E1.right")])]});
            var Q14;
            Q14=makeQuery(id+"F2.opExtrude","SWEPT_BODY",BODY,{"disambiguationData":[OSD([sQuery(id+"F0.wireOp",EDGE,"E9.bottom"),sQuery(id+"F0.wireOp",EDGE,"E9.top"),sQuery(id+"F0.wireOp",EDGE,"E9.left"),sQuery(id+"F0.wireOp",EDGE,"E9.right")])]});
            booleanBodies(context, id + "F9", {"operationType" : BooleanOperationType.SUBTRACTION, "tools" : qUnion([Q0, Q1, Q2, Q3, Q4, Q5, Q6, Q7, Q8]), "targets" : qUnion([Q9, Q10, Q11, Q12, Q13, Q14]), "keepTools" : true});
        }
        {
            var Q0;
            Q0=makeQuery(id+"F8.opExtrude","CAP_FACE",FACE,{"disambiguationData":[OSD([sQuery(id+"F7.wireOp",EDGE,"E48.bottom"),sQuery(id+"F7.wireOp",EDGE,"E48.top"),sQuery(id+"F7.wireOp",EDGE,"E48.left"),sQuery(id+"F7.wireOp",EDGE,"E48.right")])],"isStart":false});
            var sketch = newSketch(context, id + "F10", { "sketchPlane" : qUnion([Q0])});
            skCircle(sketch, "E58", {"center": v(0, 0) * mm, "radius": 457.2 * mm});
            skSolve(sketch);
        }
        {
            var Q0;
            Q0=makeQuery(id+"F10.imprint","IMPRINT",FACE,{"disambiguationData":[TD([[makeQuery(id+"F10.imprint","IMPRINT",EDGE,{"derivedFrom":sQuery(id+"F10.wireOp",EDGE,"E58")}),1.0]])]});
            var Q1;
            Q1=makeQuery(id+"F10.imprint","IMPRINT",FACE,{"disambiguationData":[TD([[makeQuery(id+"F10.imprint","IMPRINT",EDGE,{"derivedFrom":makeQuery(id+"F8.opExtrude","CAP_EDGE",EDGE,{"disambiguationData":[OSD([sQuery(id+"F7.wireOp",EDGE,"E48.bottom")])],"isStart":false})}),-1.0]])]});
            extrude(context, id + "F11", {"entities" : qUnion([Q0, Q1]), "depth" : 19.05 * mm, "offsetDistance" : 25.4 * mm});
        }
    });
